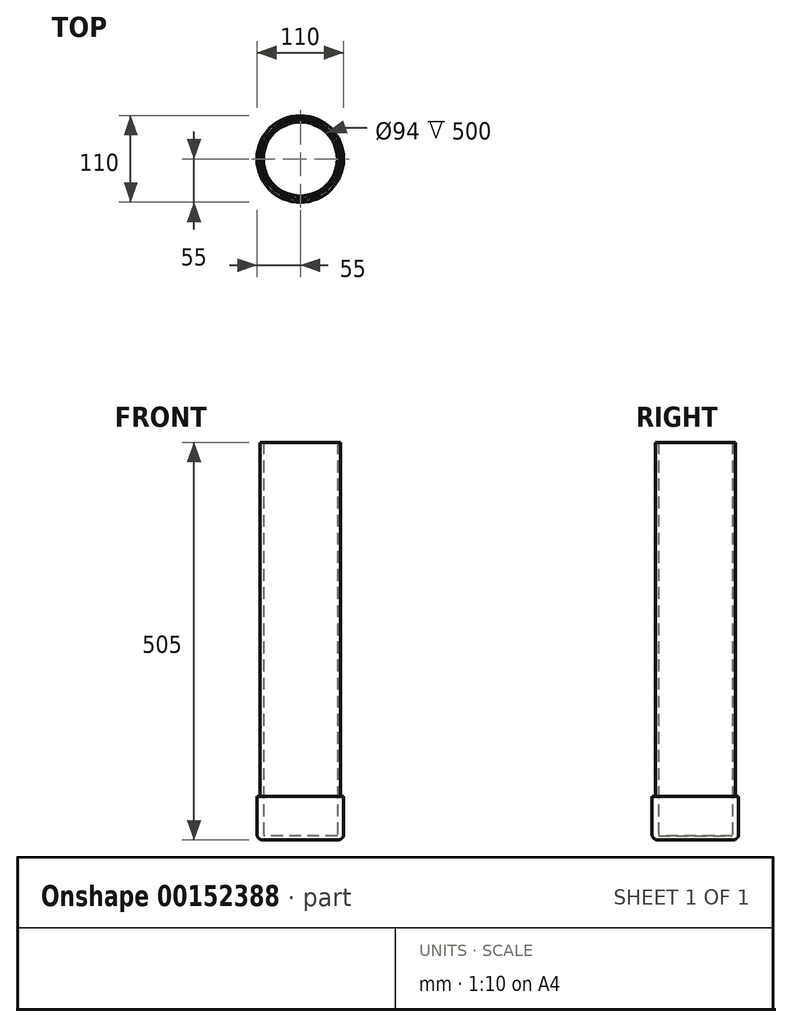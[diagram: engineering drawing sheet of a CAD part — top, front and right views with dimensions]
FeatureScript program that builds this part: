
annotation { "Feature Type Name" : "Feature", "Feature Type Description" : "" }
export const myFeature = defineFeature(function(context is Context, id is Id, definition is map)
    precondition{}
    {
        {
            var Q0;
            Q0=qCreatedBy(makeId("Top.planeOp"),FACE);
            var sketch = newSketch(context, id + "F0", { "sketchPlane" : qUnion([Q0])});
            skCircle(sketch, "E0", {"center": v(0, 0) * mm, "radius": 47 * mm});
            skCircle(sketch, "E1", {"center": v(0, 0) * mm, "radius": 51 * mm});
            skCircle(sketch, "E2", {"center": v(0, 0) * mm, "radius": 55 * mm});
            skSolve(sketch);
        }
        {
            var Q0;
            Q0=makeQuery(id+"F0.imprint","IMPRINT",FACE,{"disambiguationData":[TD([[makeQuery(id+"F0.imprint","IMPRINT",EDGE,{"derivedFrom":sQuery(id+"F0.wireOp",EDGE,"E1")}),-1.0]])]});
            var Q1;
            Q1=makeQuery(id+"F0.imprint","IMPRINT",FACE,{"disambiguationData":[TD([[makeQuery(id+"F0.imprint","IMPRINT",EDGE,{"derivedFrom":sQuery(id+"F0.wireOp",EDGE,"E0")}),-1.0]])]});
            var Q2;
            Q2=makeQuery(id+"F0.imprint","IMPRINT",FACE,{"disambiguationData":[TD([[makeQuery(id+"F0.imprint","IMPRINT",EDGE,{"derivedFrom":sQuery(id+"F0.wireOp",EDGE,"E0")}),1.0]])]});
            extrude(context, id + "F1", {"entities" : qUnion([Q0, Q1, Q2]), "oppositeDirection" : true, "depth" : 5 * mm});
        }
        {
            var Q0;
            Q0=makeQuery(id+"F0.imprint","IMPRINT",FACE,{"disambiguationData":[TD([[makeQuery(id+"F0.imprint","IMPRINT",EDGE,{"derivedFrom":sQuery(id+"F0.wireOp",EDGE,"E0")}),-1.0]])]});
            extrude(context, id + "F2", {"entities" : qUnion([Q0]), "operationType" : NewBodyOperationType.ADD, "depth" : 500 * mm});
        }
        {
            var Q0;
            Q0=makeQuery(id+"F0.imprint","IMPRINT",FACE,{"disambiguationData":[TD([[makeQuery(id+"F0.imprint","IMPRINT",EDGE,{"derivedFrom":sQuery(id+"F0.wireOp",EDGE,"E1")}),-1.0]])]});
            extrude(context, id + "F3", {"entities" : qUnion([Q0]), "operationType" : NewBodyOperationType.ADD, "depth" : 50 * mm});
        }
        {
            var Q0;
            Q0=makeQuery(id+"F1.opExtrude","CAP_EDGE",EDGE,{"disambiguationData":[OSD([sQuery(id+"F0.wireOp",EDGE,"E2")])],"isStart":false});
            fillet(context, id + "F4", {"entities" : qUnion([Q0]), "radius" : 7 * mm, "tangentPropagation" : true, "allowEdgeOverflow" : false});
        }
    });
